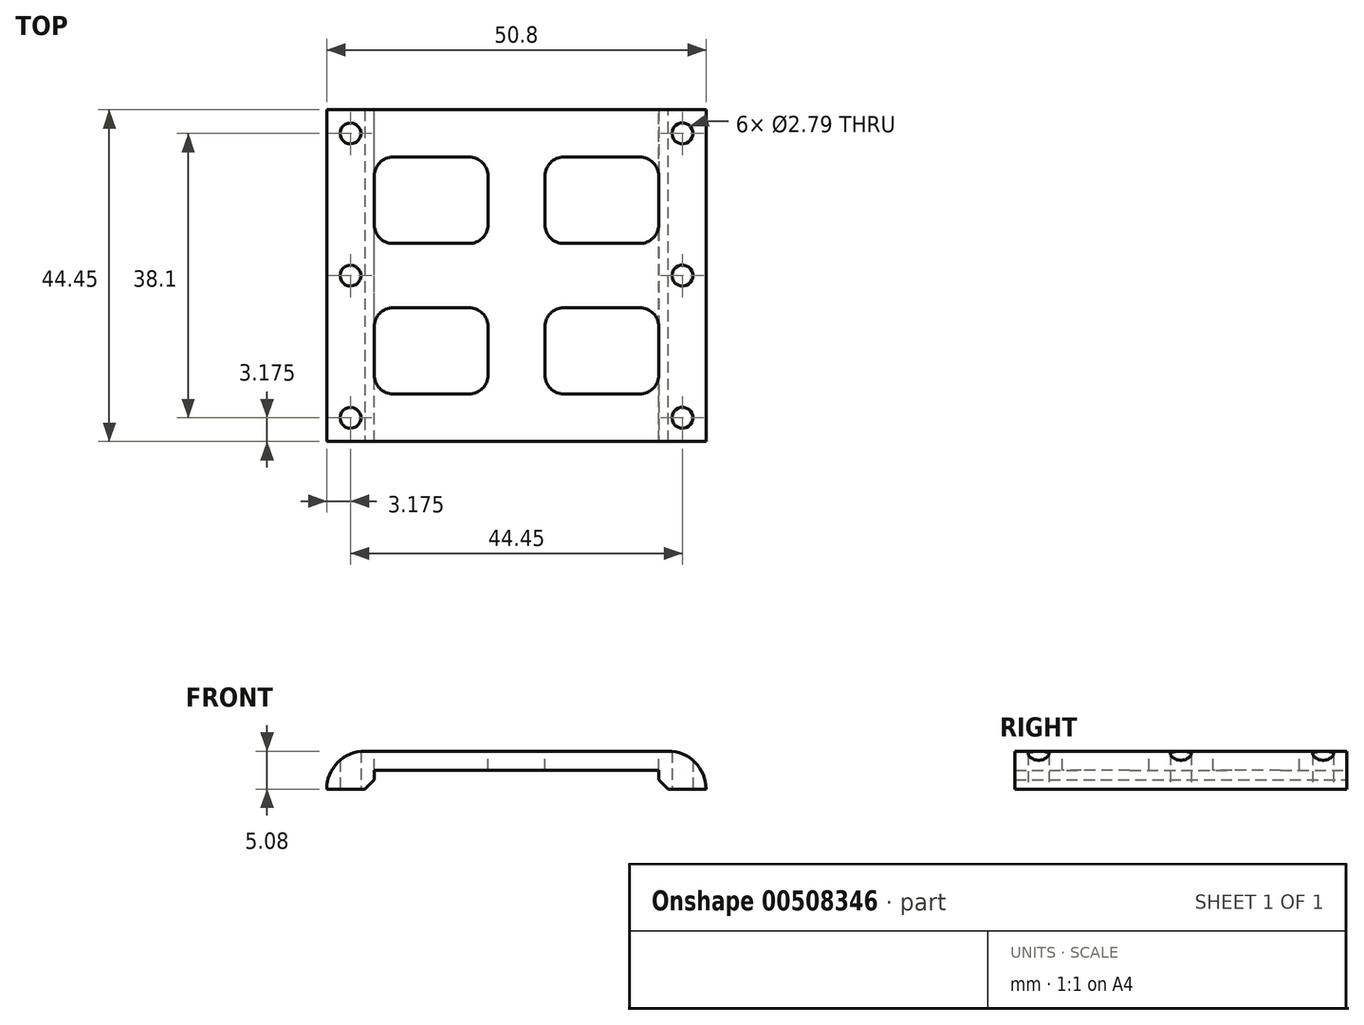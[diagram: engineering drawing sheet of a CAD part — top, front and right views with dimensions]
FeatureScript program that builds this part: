
annotation { "Feature Type Name" : "Feature", "Feature Type Description" : "" }
export const myFeature = defineFeature(function(context is Context, id is Id, definition is map)
    precondition{}
    {
        {
            var Q0;
            Q0=qCreatedBy(makeId("Front.planeOp"),FACE);
            var sketch = newSketch(context, id + "F0", { "sketchPlane" : qUnion([Q0])});
            skLineSegment(sketch, "E0.bottom", {"start": v(-25.4, 1.27) * mm, "end": v(25.4, 1.27) * mm});
            skLineSegment(sketch, "E0.top", {"start": v(-19.05, -1.27) * mm, "end": v(19.05, -1.27) * mm});
            skLineSegment(sketch, "E0.left", {"start": v(-25.4, 1.27) * mm, "end": v(-25.4, -1.27) * mm});
            skLineSegment(sketch, "E0.right", {"start": v(25.4, 1.27) * mm, "end": v(25.4, -1.27) * mm});
            skPoint(sketch, "E0.middle", {"position": v(0, 0) * mm});
            skLineSegment(sketch, "E1.top", {"start": v(-25.4, -3.81) * mm, "end": v(-19.05, -3.81) * mm});
            skLineSegment(sketch, "E1.left", {"start": v(-25.4, -1.27) * mm, "end": v(-25.4, -3.81) * mm});
            skLineSegment(sketch, "E1.right", {"start": v(-19.05, -1.27) * mm, "end": v(-19.05, -3.81) * mm});
            skLineSegment(sketch, "E2", {"start": v(0, 0) * mm, "end": v(0, 1.27) * mm});
            skLineSegment(sketch, "E3.MirrorCS", {"start": v(25.4, -1.27) * mm, "end": v(25.4, -3.81) * mm});
            skLineSegment(sketch, "E4.MirrorCS", {"start": v(19.05, -1.27) * mm, "end": v(19.05, -3.8) * mm});
            skLineSegment(sketch, "E5.MirrorCS", {"start": v(25.4, -3.8) * mm, "end": v(19.05, -3.8) * mm});
            skSolve(sketch);
        }
        {
            var Q0;
            Q0 = qSketchRegion(id + "F0", true);
            extrude(context, id + "F1", {"entities" : qUnion([Q0]), "depth" : 44.45 * mm});
        }
        {
            var Q0;
            Q0=makeQuery(id+"F1.opExtrude","SWEPT_EDGE",EDGE,{"disambiguationData":[OSD([sQuery(id+"F0.wireOp",EDGE,"E0.bottom"),sQuery(id+"F0.wireOp",EDGE,"E0.left")])]});
            var Q1;
            Q1=makeQuery(id+"F1.opExtrude","SWEPT_EDGE",EDGE,{"disambiguationData":[OSD([sQuery(id+"F0.wireOp",EDGE,"E0.bottom"),sQuery(id+"F0.wireOp",EDGE,"E0.right")])]});
            fillet(context, id + "F2", {"entities" : qUnion([Q0, Q1]), "radius" : 5.08 * mm, "tangentPropagation" : true, "allowEdgeOverflow" : false});
        }
        {
            var Q0;
            Q0=makeQuery(id+"F1.opExtrude","SWEPT_FACE",FACE,{"disambiguationData":[OSD([sQuery(id+"F0.wireOp",EDGE,"E1.top")])]});
            var sketch = newSketch(context, id + "F3", { "sketchPlane" : qUnion([Q0])});
            skLineSegment(sketch, "E6", {"start": v(0, 0) * mm, "end": v(0, 44.45) * mm});
            skLineSegment(sketch, "E7", {"start": v(0, 22.23) * mm, "end": v(-22.22, 22.23) * mm});
            skPoint(sketch, "E7.endSnap0", {"position": v(0, 22.23) * mm});
            skLineSegment(sketch, "E8", {"start": v(-22.23, 22.23) * mm, "end": v(-22.23, 41.28) * mm});
            skCircle(sketch, "E9", {"center": v(-22.22, 41.28) * mm, "radius": 1.4 * mm});
            skLineSegment(sketch, "E10", {"start": v(-22.23, 41.28) * mm, "end": v(-22.23, 44.45) * mm});
            skCircle(sketch, "E11.MirrorC", {"center": v(-22.22, 3.17) * mm, "radius": 1.4 * mm});
            skCircle(sketch, "E12.MirrorC", {"center": v(22.22, 41.28) * mm, "radius": 1.4 * mm});
            skCircle(sketch, "E13.MirrorC", {"center": v(22.22, 3.17) * mm, "radius": 1.4 * mm});
            skCircle(sketch, "E14", {"center": v(-22.22, 22.23) * mm, "radius": 1.4 * mm});
            skCircle(sketch, "E15.MirrorC", {"center": v(22.22, 22.23) * mm, "radius": 1.4 * mm});
            skSolve(sketch);
        }
        {
            var Q0;
            Q0 = qSketchRegion(id + "F3", true);
            extrude(context, id + "F4", {"entities" : qUnion([Q0]), "operationType" : NewBodyOperationType.REMOVE, "oppositeDirection" : true, "depth" : 25.4 * mm});
        }
        {
            var Q0;
            Q0=makeQuery(id+"F1.opExtrude","SWEPT_FACE",FACE,{"disambiguationData":[OSD([sQuery(id+"F0.wireOp",EDGE,"E0.bottom")])]});
            var sketch = newSketch(context, id + "F5", { "sketchPlane" : qUnion([Q0])});
            skLineSegment(sketch, "E16.bottom", {"start": v(19.05, -6.35) * mm, "end": v(-19.05, -6.35) * mm});
            skLineSegment(sketch, "E16.top", {"start": v(19.05, -38.1) * mm, "end": v(-19.05, -38.1) * mm});
            skLineSegment(sketch, "E16.left", {"start": v(19.05, -6.35) * mm, "end": v(19.05, -38.1) * mm});
            skLineSegment(sketch, "E16.right", {"start": v(-19.05, -6.35) * mm, "end": v(-19.05, -38.1) * mm});
            skPoint(sketch, "E16.middle", {"position": v(0, -22.23) * mm});
            skPoint(sketch, "E16.middle.positionSnap0", {"position": v(20.32, -22.23) * mm});
            skPoint(sketch, "E16.centerSnap0", {"position": v(20.32, -22.23) * mm});
            skLineSegment(sketch, "E17", {"start": v(0, 0) * mm, "end": v(0, -6.35) * mm});
            skLineSegment(sketch, "E18.bottom", {"start": v(3.8, -6.35) * mm, "end": v(-3.81, -6.35) * mm});
            skLineSegment(sketch, "E18.top", {"start": v(3.8, -38.1) * mm, "end": v(-3.81, -38.1) * mm});
            skLineSegment(sketch, "E18.left", {"start": v(3.81, -6.35) * mm, "end": v(3.81, -17.93) * mm});
            skLineSegment(sketch, "E18.right", {"start": v(-3.81, -6.35) * mm, "end": v(-3.81, -17.93) * mm});
            skLineSegment(sketch, "E19.bottom", {"start": v(19.05, -17.93) * mm, "end": v(3.81, -17.93) * mm});
            skLineSegment(sketch, "E19.top", {"start": v(19.05, -26.52) * mm, "end": v(3.81, -26.52) * mm});
            skLineSegment(sketch, "E19.left", {"start": v(19.05, -17.93) * mm, "end": v(19.05, -26.52) * mm});
            skLineSegment(sketch, "E19.right", {"start": v(-19.05, -17.93) * mm, "end": v(-19.05, -26.52) * mm});
            skLineSegment(sketch, "E20.trimOffspring", {"start": v(3.81, -26.52) * mm, "end": v(3.81, -38.1) * mm});
            skLineSegment(sketch, "E21.trimOffspring", {"start": v(-3.81, -17.93) * mm, "end": v(-19.05, -17.93) * mm});
            skLineSegment(sketch, "E22.trimOffspring", {"start": v(-3.81, -26.52) * mm, "end": v(-19.05, -26.52) * mm});
            skLineSegment(sketch, "E23.trimOffspring", {"start": v(-3.81, -26.52) * mm, "end": v(-3.81, -38.1) * mm});
            skLineSegment(sketch, "E24", {"start": v(0, -22.23) * mm, "end": v(-20.32, -22.23) * mm});
            skSolve(sketch);
        }
        {
            var Q0;
            {var subQ3=sQuery(id+"F5.wireOp",EDGE,"E18.left");Q0=makeQuery(id+"F5.imprint","IMPRINT",FACE,{"disambiguationData":[TD([[makeQuery(id+"F5.imprint","IMPRINT",EDGE,{"derivedFrom":subQ3}),1.0]])]});}
            var Q1;
            {var subQ3=sQuery(id+"F5.wireOp",EDGE,"E18.right");Q1=makeQuery(id+"F5.imprint","IMPRINT",FACE,{"disambiguationData":[TD([[makeQuery(id+"F5.imprint","IMPRINT",EDGE,{"derivedFrom":subQ3}),-1.0]])]});}
            var Q2;
            {var subQ4=sQuery(id+"F5.wireOp",EDGE,"E19.top");Q2=makeQuery(id+"F5.imprint","IMPRINT",FACE,{"disambiguationData":[TD([[makeQuery(id+"F5.imprint","IMPRINT",EDGE,{"derivedFrom":subQ4}),1.0]])]});}
            var Q3;
            {var subQ4=sQuery(id+"F5.wireOp",EDGE,"E22.trimOffspring");Q3=makeQuery(id+"F5.imprint","IMPRINT",FACE,{"disambiguationData":[TD([[makeQuery(id+"F5.imprint","IMPRINT",EDGE,{"derivedFrom":subQ4}),1.0]])]});}
            extrude(context, id + "F6", {"entities" : qUnion([Q0, Q1, Q2, Q3]), "operationType" : NewBodyOperationType.REMOVE, "oppositeDirection" : true, "depth" : 25.4 * mm});
        }
        {
            var Q0;
            Q0=makeQuery(id+"F6.boolean.opBoolean","COPY",EDGE,{"derivedFrom":makeQuery(id+"F6.opExtrude","SWEPT_EDGE",EDGE,{"disambiguationData":[OSD([sQuery(id+"F5.wireOp",EDGE,"E16.bottom"),sQuery(id+"F5.wireOp",EDGE,"E16.right")])]})});
            var Q1;
            Q1=makeQuery(id+"F6.boolean.opBoolean","COPY",EDGE,{"derivedFrom":makeQuery(id+"F6.opExtrude","SWEPT_EDGE",EDGE,{"disambiguationData":[OSD([sQuery(id+"F5.wireOp",EDGE,"E18.right"),sQuery(id+"F5.wireOp",EDGE,"E21.trimOffspring")])]})});
            var Q2;
            Q2=makeQuery(id+"F6.boolean.opBoolean","COPY",EDGE,{"derivedFrom":makeQuery(id+"F6.opExtrude","SWEPT_EDGE",EDGE,{"disambiguationData":[OSD([sQuery(id+"F5.wireOp",EDGE,"E16.bottom"),sQuery(id+"F5.wireOp",EDGE,"E18.bottom"),sQuery(id+"F5.wireOp",EDGE,"E18.right")])]})});
            var Q3;
            Q3=makeQuery(id+"F6.boolean.opBoolean","COPY",EDGE,{"derivedFrom":makeQuery(id+"F6.opExtrude","SWEPT_EDGE",EDGE,{"disambiguationData":[OSD([sQuery(id+"F5.wireOp",EDGE,"E16.right"),sQuery(id+"F5.wireOp",EDGE,"E19.right"),sQuery(id+"F5.wireOp",EDGE,"E21.trimOffspring")])]})});
            var Q4;
            Q4=makeQuery(id+"F6.boolean.opBoolean","COPY",EDGE,{"derivedFrom":makeQuery(id+"F6.opExtrude","SWEPT_EDGE",EDGE,{"disambiguationData":[OSD([sQuery(id+"F5.wireOp",EDGE,"E16.top"),sQuery(id+"F5.wireOp",EDGE,"E16.right")])]})});
            var Q5;
            Q5=makeQuery(id+"F6.boolean.opBoolean","COPY",EDGE,{"derivedFrom":makeQuery(id+"F6.opExtrude","SWEPT_EDGE",EDGE,{"disambiguationData":[OSD([sQuery(id+"F5.wireOp",EDGE,"E16.top"),sQuery(id+"F5.wireOp",EDGE,"E18.top"),sQuery(id+"F5.wireOp",EDGE,"E20.trimOffspring")])]})});
            var Q6;
            Q6=makeQuery(id+"F6.boolean.opBoolean","COPY",EDGE,{"derivedFrom":makeQuery(id+"F6.opExtrude","SWEPT_EDGE",EDGE,{"disambiguationData":[OSD([sQuery(id+"F5.wireOp",EDGE,"E18.left"),sQuery(id+"F5.wireOp",EDGE,"E19.bottom")])]})});
            var Q7;
            Q7=makeQuery(id+"F6.boolean.opBoolean","COPY",EDGE,{"derivedFrom":makeQuery(id+"F6.opExtrude","SWEPT_EDGE",EDGE,{"disambiguationData":[OSD([sQuery(id+"F5.wireOp",EDGE,"E16.bottom"),sQuery(id+"F5.wireOp",EDGE,"E18.bottom"),sQuery(id+"F5.wireOp",EDGE,"E18.left")])]})});
            var Q8;
            Q8=makeQuery(id+"F6.boolean.opBoolean","COPY",EDGE,{"derivedFrom":makeQuery(id+"F6.opExtrude","SWEPT_EDGE",EDGE,{"disambiguationData":[OSD([sQuery(id+"F5.wireOp",EDGE,"E16.right"),sQuery(id+"F5.wireOp",EDGE,"E19.right"),sQuery(id+"F5.wireOp",EDGE,"E22.trimOffspring")])]})});
            var Q9;
            Q9=makeQuery(id+"F6.boolean.opBoolean","COPY",EDGE,{"derivedFrom":makeQuery(id+"F6.opExtrude","SWEPT_EDGE",EDGE,{"disambiguationData":[OSD([sQuery(id+"F5.wireOp",EDGE,"E19.top"),sQuery(id+"F5.wireOp",EDGE,"E20.trimOffspring")])]})});
            var Q10;
            Q10=makeQuery(id+"F6.boolean.opBoolean","COPY",EDGE,{"derivedFrom":makeQuery(id+"F6.opExtrude","SWEPT_EDGE",EDGE,{"disambiguationData":[OSD([sQuery(id+"F5.wireOp",EDGE,"E16.left"),sQuery(id+"F5.wireOp",EDGE,"E19.top"),sQuery(id+"F5.wireOp",EDGE,"E19.left")])]})});
            var Q11;
            Q11=makeQuery(id+"F6.boolean.opBoolean","COPY",EDGE,{"derivedFrom":makeQuery(id+"F6.opExtrude","SWEPT_EDGE",EDGE,{"disambiguationData":[OSD([sQuery(id+"F5.wireOp",EDGE,"E22.trimOffspring"),sQuery(id+"F5.wireOp",EDGE,"E23.trimOffspring")])]})});
            var Q12;
            Q12=makeQuery(id+"F6.boolean.opBoolean","COPY",EDGE,{"derivedFrom":makeQuery(id+"F6.opExtrude","SWEPT_EDGE",EDGE,{"disambiguationData":[OSD([sQuery(id+"F5.wireOp",EDGE,"E16.bottom"),sQuery(id+"F5.wireOp",EDGE,"E16.left")])]})});
            var Q13;
            Q13=makeQuery(id+"F6.boolean.opBoolean","COPY",EDGE,{"derivedFrom":makeQuery(id+"F6.opExtrude","SWEPT_EDGE",EDGE,{"disambiguationData":[OSD([sQuery(id+"F5.wireOp",EDGE,"E16.left"),sQuery(id+"F5.wireOp",EDGE,"E19.bottom"),sQuery(id+"F5.wireOp",EDGE,"E19.left")])]})});
            var Q14;
            Q14=makeQuery(id+"F6.boolean.opBoolean","COPY",EDGE,{"derivedFrom":makeQuery(id+"F6.opExtrude","SWEPT_EDGE",EDGE,{"disambiguationData":[OSD([sQuery(id+"F5.wireOp",EDGE,"E16.top"),sQuery(id+"F5.wireOp",EDGE,"E16.left")])]})});
            var Q15;
            Q15=makeQuery(id+"F6.boolean.opBoolean","COPY",EDGE,{"derivedFrom":makeQuery(id+"F6.opExtrude","SWEPT_EDGE",EDGE,{"disambiguationData":[OSD([sQuery(id+"F5.wireOp",EDGE,"E16.top"),sQuery(id+"F5.wireOp",EDGE,"E18.top"),sQuery(id+"F5.wireOp",EDGE,"E23.trimOffspring")])]})});
            fillet(context, id + "F7", {"entities" : qUnion([Q0, Q1, Q2, Q3, Q4, Q5, Q6, Q7, Q8, Q9, Q10, Q11, Q12, Q13, Q14, Q15]), "radius" : 2.54 * mm, "tangentPropagation" : true, "allowEdgeOverflow" : false});
        }
        {
            var Q0;
            {var subQ0=sQuery(id+"F5.wireOp",EDGE,"E16.left");Q0=makeQuery(id+"F6.boolean.opBoolean","INTERSECT",EDGE,{"derivedFrom":[makeQuery(id+"F6.opExtrude","SWEPT_FACE",FACE,{"disambiguationData":[OSD([subQ0]),TDD([makeQuery(id+"F5.imprint","IMPRINT",EDGE,{"disambiguationData":[TD([[makeQuery(id+"F5.imprint","INTERSECT",VERTEX,{"derivedFrom":[sQuery(id+"F5.wireOp",EDGE,"E16.bottom"),subQ0]}),-1.0]])],"derivedFrom":subQ0})])]}),makeQuery(id+"F6.opExtrude","SWEPT_FACE",FACE,{"disambiguationData":[OSD([subQ0]),TDD([makeQuery(id+"F5.imprint","IMPRINT",EDGE,{"disambiguationData":[TD([[makeQuery(id+"F5.imprint","INTERSECT",VERTEX,{"derivedFrom":[sQuery(id+"F5.wireOp",EDGE,"E16.top"),subQ0]}),1.0]])],"derivedFrom":subQ0})])]})]});}
            var Q1;
            {var subQ0=sQuery(id+"F5.wireOp",EDGE,"E16.right");Q1=makeQuery(id+"F6.boolean.opBoolean","INTERSECT",EDGE,{"derivedFrom":[makeQuery(id+"F6.opExtrude","SWEPT_FACE",FACE,{"disambiguationData":[OSD([subQ0]),TDD([makeQuery(id+"F5.imprint","IMPRINT",EDGE,{"disambiguationData":[TD([[makeQuery(id+"F5.imprint","INTERSECT",VERTEX,{"derivedFrom":[sQuery(id+"F5.wireOp",EDGE,"E16.bottom"),subQ0]}),-1.0]])],"derivedFrom":subQ0})])]}),makeQuery(id+"F6.opExtrude","SWEPT_FACE",FACE,{"disambiguationData":[OSD([subQ0]),TDD([makeQuery(id+"F5.imprint","IMPRINT",EDGE,{"disambiguationData":[TD([[makeQuery(id+"F5.imprint","INTERSECT",VERTEX,{"derivedFrom":[sQuery(id+"F5.wireOp",EDGE,"E16.top"),subQ0]}),1.0]])],"derivedFrom":subQ0})])]})]});}
            chamfer(context, id + "F8", {"entities" : qUnion([Q0, Q1]), "width" : 1.27 * mm, "tangentPropagation" : true});
        }
    });
